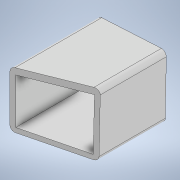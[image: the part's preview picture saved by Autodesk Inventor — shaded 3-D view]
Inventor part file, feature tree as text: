
AUTODESK INVENTOR PART (.ipt)
format: ipt  version: 2021 (Build 250183000, 183)  size: 139,776 bytes
history: native  units: mm
features: extrude x2, sketch x2, fillet x1, projected_geometry x1
ambient origin geometry x8: Origin, YZ Plane, XZ Plane, XY Plane, X Axis, Y Axis, Z Axis, Center Point
bodies: Volumenkörper1 (feature_tree)
feature tree (6):
  extrude  "Extrusion1"  Depth=40.3mm
  extrude  "Extrusion3"  Depth=3.0mm
  fillet  "Rundung1"  Radius=16.755161mm
  sketch  "Skizze1"  dims[d1=29.5mm d2=40.3mm]
  sketch  "Skizze3"  dims[d6=90.0deg d9=15.882496mm d12=16.755161mm d13=41.115174mm d14=33.802854mm d15=57.0mm d16=0.0mm d22=4.0mm d23=3.0mm d24=3.0mm d25=3.0mm d27=13.264502mm d28=57.0mm d29=0.0mm d30=15.184364mm d31=3.0mm]
  projected_geometry  "Projizierte Kontur2"
